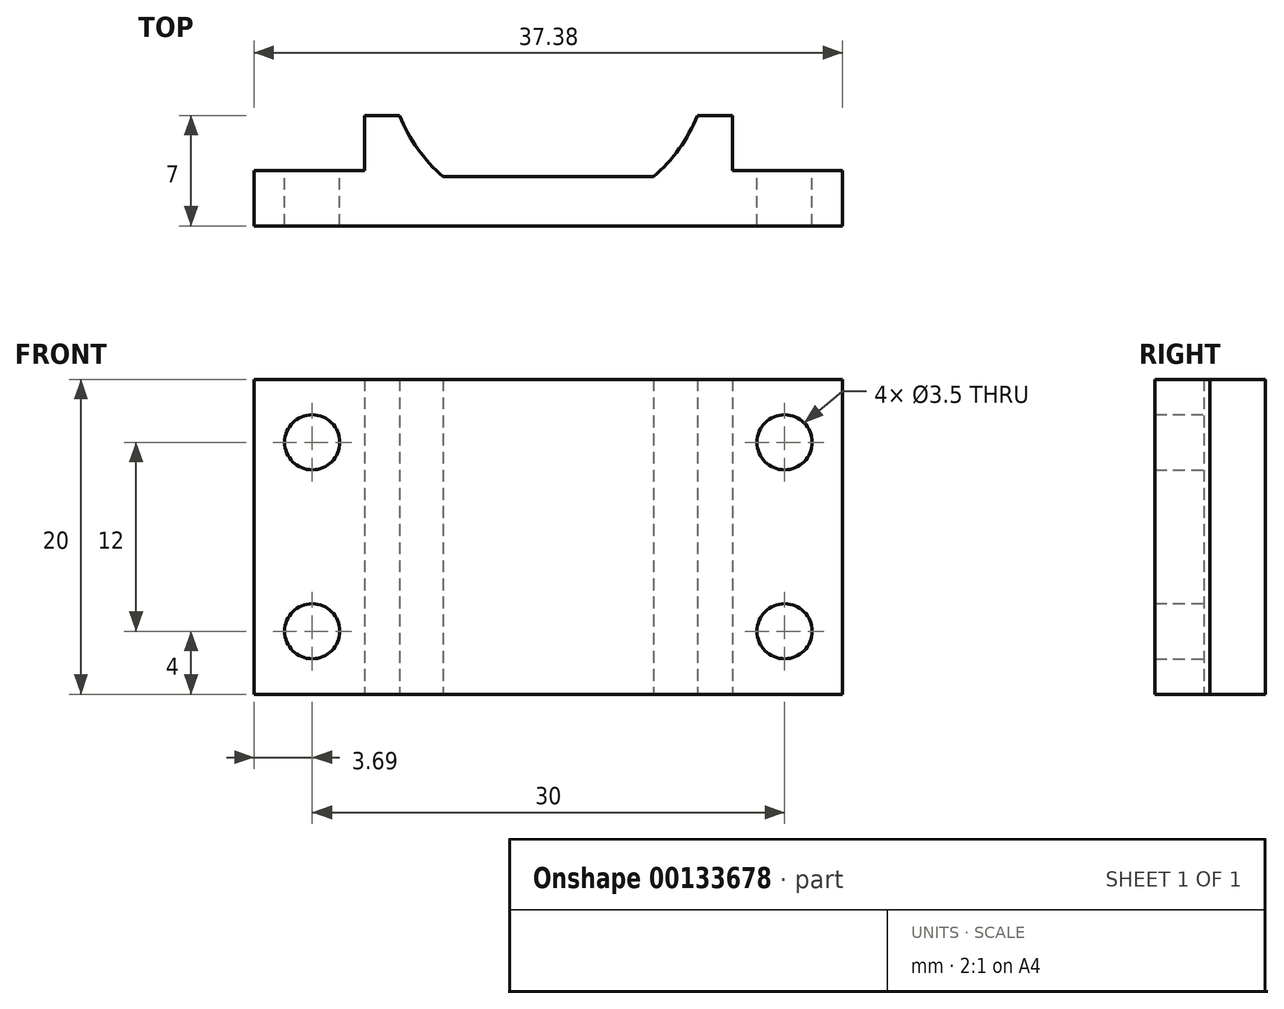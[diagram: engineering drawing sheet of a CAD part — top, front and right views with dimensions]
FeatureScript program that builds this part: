
annotation { "Feature Type Name" : "Feature", "Feature Type Description" : "" }
export const myFeature = defineFeature(function(context is Context, id is Id, definition is map)
    precondition{}
    {
        {
            var Q0;
            Q0=qCreatedBy(makeId("Top.planeOp"),FACE);
            var sketch = newSketch(context, id + "F0", { "sketchPlane" : qUnion([Q0])});
            skArc(sketch, "E0", {"start": v(-9.46, -3.82) * mm, "mid": v(-8.3, -5.93) * mm, "end": v(-6.69, -7.7) * mm});
            skLineSegment(sketch, "E1.top", {"start": v(-6.69, -7.7) * mm, "end": v(6.69, -7.7) * mm});
            skArc(sketch, "E2.trimOffspring", {"start": v(6.69, -7.7) * mm, "mid": v(8.3, -5.93) * mm, "end": v(9.46, -3.82) * mm});
            skLineSegment(sketch, "E3", {"start": v(-11.69, -7.32) * mm, "end": v(-18.69, -7.32) * mm});
            skLineSegment(sketch, "E4", {"start": v(-18.69, -7.32) * mm, "end": v(-18.69, -10.82) * mm});
            skLineSegment(sketch, "E5", {"start": v(-18.69, -10.82) * mm, "end": v(18.69, -10.82) * mm});
            skLineSegment(sketch, "E6", {"start": v(18.69, -10.82) * mm, "end": v(18.69, -7.32) * mm});
            skLineSegment(sketch, "E7", {"start": v(18.69, -7.32) * mm, "end": v(11.69, -7.32) * mm});
            skLineSegment(sketch, "E8", {"start": v(0, -10.82) * mm, "end": v(0, 0) * mm, "construction": true});
            skPoint(sketch, "E8.endSnap0", {"position": v(0, -7.7) * mm});
            skLineSegment(sketch, "E9", {"start": v(-11.69, -3.82) * mm, "end": v(-9.46, -3.82) * mm});
            skLineSegment(sketch, "E10", {"start": v(-11.69, -7.32) * mm, "end": v(-11.69, -3.82) * mm});
            skLineSegment(sketch, "E11", {"start": v(11.69, -7.32) * mm, "end": v(11.69, -3.82) * mm});
            skLineSegment(sketch, "E12.trimOffspring", {"start": v(9.46, -3.82) * mm, "end": v(11.69, -3.82) * mm});
            skSolve(sketch);
        }
        {
            var Q0;
            Q0=makeQuery(id+"F0.imprint","IMPRINT",FACE,{"disambiguationData":[TD([[makeQuery(id+"F0.imprint","IMPRINT",EDGE,{"derivedFrom":sQuery(id+"F0.wireOp",EDGE,"E0")}),-1.0]])]});
            extrude(context, id + "F1", {"entities" : qUnion([Q0]), "depth" : 20 * mm});
        }
        {
            var Q0;
            Q0 = qSketchRegion(id + "F0", true);
            extrude(context, id + "F2", {"entities" : qUnion([Q0]), "operationType" : NewBodyOperationType.ADD, "depth" : 2 * mm});
        }
        {
            var Q0;
            Q0=makeQuery(id+"F1.opExtrude","SWEPT_FACE",FACE,{"disambiguationData":[OSD([sQuery(id+"F0.wireOp",EDGE,"E7")])]});
            var sketch = newSketch(context, id + "F3", { "sketchPlane" : qUnion([Q0])});
            skLineSegment(sketch, "E13", {"start": v(-15, 16) * mm, "end": v(-15, 4) * mm});
            skCircle(sketch, "E14", {"center": v(-15, 16) * mm, "radius": 1.75 * mm});
            skCircle(sketch, "E15", {"center": v(-15, 4) * mm, "radius": 1.75 * mm});
            skLineSegment(sketch, "E16", {"start": v(-15, 16) * mm, "end": v(15, 16) * mm});
            skLineSegment(sketch, "E17", {"start": v(-15, 4) * mm, "end": v(15, 4) * mm});
            skCircle(sketch, "E18", {"center": v(15, 16) * mm, "radius": 1.75 * mm});
            skCircle(sketch, "E19", {"center": v(15, 4) * mm, "radius": 1.75 * mm});
            skLineSegment(sketch, "E20", {"start": v(0, 4) * mm, "end": v(0, 0) * mm});
            skSolve(sketch);
        }
        {
            var Q0;
            Q0 = qSketchRegion(id + "F3", true);
            extrude(context, id + "F4", {"entities" : qUnion([Q0]), "operationType" : NewBodyOperationType.REMOVE, "oppositeDirection" : true, "depth" : 25 * mm});
        }
    });
